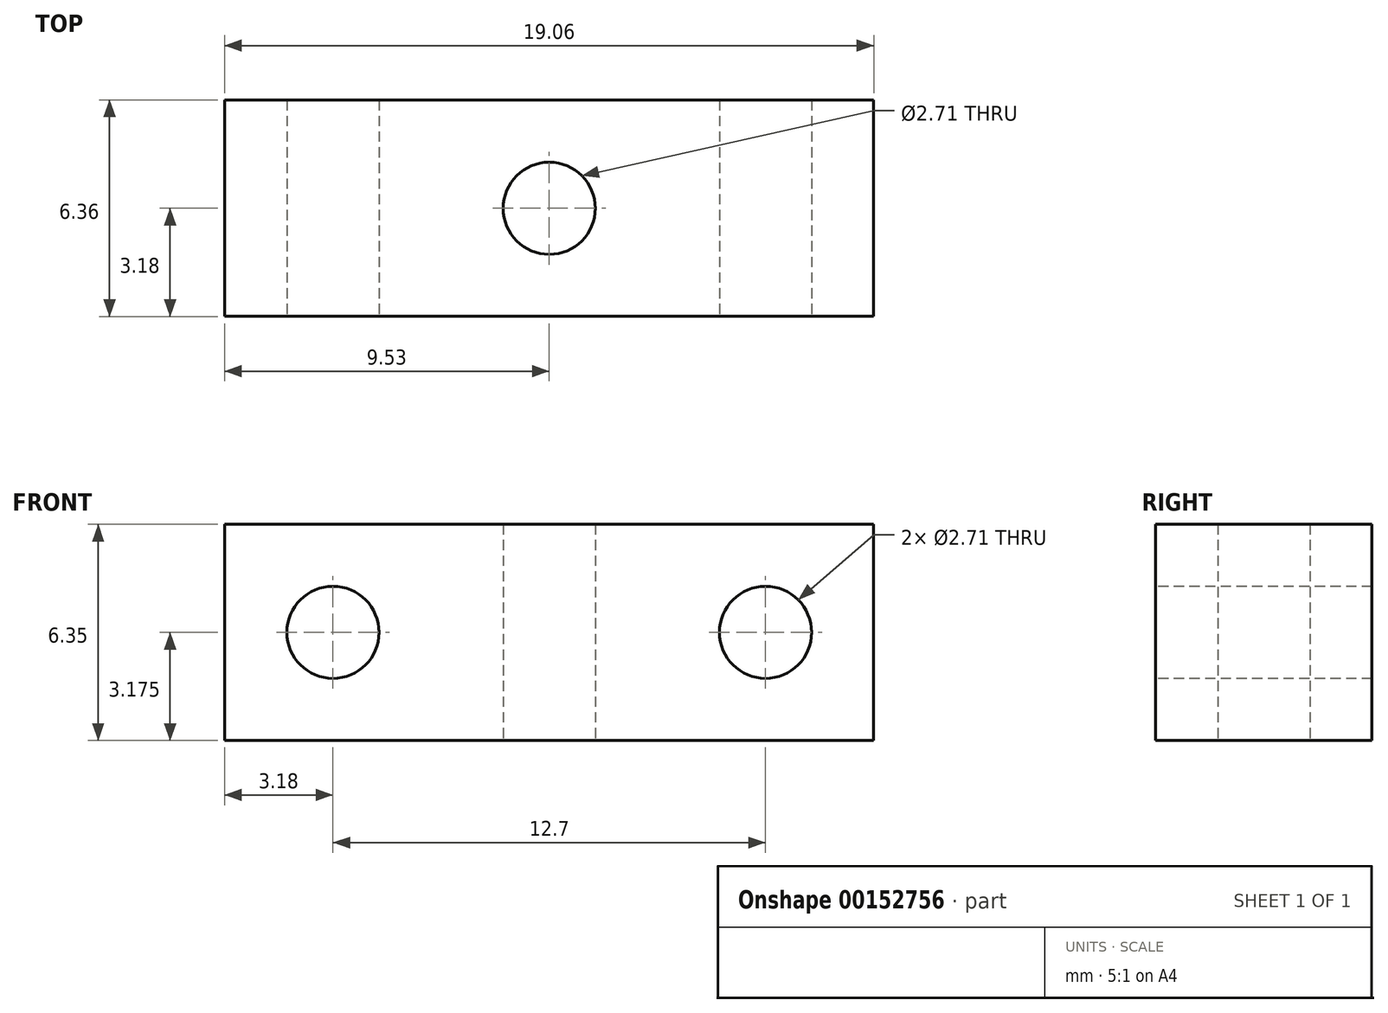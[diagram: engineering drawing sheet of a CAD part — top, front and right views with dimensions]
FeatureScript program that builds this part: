
annotation { "Feature Type Name" : "Feature", "Feature Type Description" : "" }
export const myFeature = defineFeature(function(context is Context, id is Id, definition is map)
    precondition{}
    {
        {
            var Q0;
            Q0=qCreatedBy(makeId("Top.planeOp"),FACE);
            var sketch = newSketch(context, id + "F0", { "sketchPlane" : qUnion([Q0])});
            skLineSegment(sketch, "E0.bottom", {"start": v(9.53, -3.18) * mm, "end": v(-9.53, -3.18) * mm});
            skLineSegment(sketch, "E0.top", {"start": v(9.53, 3.18) * mm, "end": v(-9.53, 3.18) * mm});
            skLineSegment(sketch, "E0.left", {"start": v(9.53, -3.18) * mm, "end": v(9.53, 3.17) * mm});
            skLineSegment(sketch, "E0.right", {"start": v(-9.53, -3.18) * mm, "end": v(-9.53, 3.17) * mm});
            skPoint(sketch, "E0.middle", {"position": v(0, 0) * mm});
            skCircle(sketch, "E1", {"center": v(0, 0) * mm, "radius": 1.35 * mm});
            skSolve(sketch);
        }
        {
            var Q0;
            Q0 = qSketchRegion(id + "F0", true);
            extrude(context, id + "F1", {"entities" : qUnion([Q0]), "depth" : 6.35 * mm});
        }
        {
            var Q0;
            Q0=makeQuery(id+"F1.opExtrude","SWEPT_FACE",FACE,{"disambiguationData":[OSD([sQuery(id+"F0.wireOp",EDGE,"E0.bottom")])]});
            var sketch = newSketch(context, id + "F2", { "sketchPlane" : qUnion([Q0])});
            skLineSegment(sketch, "E2.bottom", {"start": v(-9.53, 3.18) * mm, "end": v(-6.35, 3.18) * mm, "construction": true});
            skLineSegment(sketch, "E2.top", {"start": v(-9.53, 6.35) * mm, "end": v(-6.35, 6.35) * mm, "construction": true});
            skLineSegment(sketch, "E2.left", {"start": v(-9.53, 3.18) * mm, "end": v(-9.53, 6.35) * mm, "construction": true});
            skLineSegment(sketch, "E2.right", {"start": v(-6.35, 3.18) * mm, "end": v(-6.35, 6.35) * mm, "construction": true});
            skLineSegment(sketch, "E3.bottom", {"start": v(9.53, 3.18) * mm, "end": v(6.35, 3.18) * mm, "construction": true});
            skLineSegment(sketch, "E3.top", {"start": v(9.53, 6.35) * mm, "end": v(6.35, 6.35) * mm, "construction": true});
            skLineSegment(sketch, "E3.left", {"start": v(9.53, 3.18) * mm, "end": v(9.53, 6.35) * mm, "construction": true});
            skLineSegment(sketch, "E3.right", {"start": v(6.35, 3.18) * mm, "end": v(6.35, 6.35) * mm, "construction": true});
            skCircle(sketch, "E4", {"center": v(-6.35, 3.18) * mm, "radius": 1.35 * mm});
            skCircle(sketch, "E5", {"center": v(6.35, 3.18) * mm, "radius": 1.35 * mm});
            skSolve(sketch);
        }
        {
            var Q0;
            Q0 = qSketchRegion(id + "F2", true);
            var Q1;
            Q1=makeQuery(id+"F1.opExtrude","SWEPT_FACE",FACE,{"disambiguationData":[OSD([sQuery(id+"F0.wireOp",EDGE,"E0.top")])]});
            extrude(context, id + "F3", {"entities" : qUnion([Q0]), "operationType" : NewBodyOperationType.REMOVE, "endBound" : BoundingType.UP_TO_SURFACE, "oppositeDirection" : true, "endBoundEntityFace" : qUnion([Q1]), "depth" : 25.4 * mm});
        }
    });
